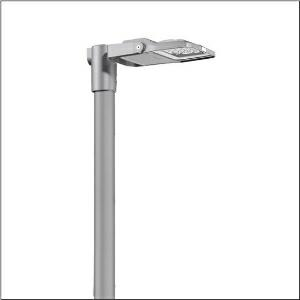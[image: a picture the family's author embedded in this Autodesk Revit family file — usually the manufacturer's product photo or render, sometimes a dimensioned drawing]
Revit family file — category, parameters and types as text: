
# Revit family: floodlight_fl_21_iq_micro___pl61_5xa7762a4c3a_196d
name_source: partatom
category: Lighting Fixtures
units: mm (PartAtom-declared; Revit-internal decimal feet)

## family parameters
Cut with Voids When Loaded = No
Host = Face
Light Source = No
Part Type = Normal
Room Calculation Point = No
Round Connector Dimension = Use Diameter
Shared = No

## types (1)
- --- (1 x LED, 3030 lm, 23.1 W, 4000K)
    Apparent Load = 23 VA
    CIE Flux Codes = 33 65 98 100 100
    Color Rendering = 70
    Color Temperature = 4000K
    Default Elevation = 1800 mm
    Description = Floodlight FL 21 iQ micro, floodlight, primary light control with lens, of PMMA, primary optical cover: protective disc, of toughened safety glass, transparent, light distribution: PL61, light emission: direct distribution, installation type: surface-mounted, lamps: LED, High Power LED, rated values: 3.030lm | 23,1W | 131,2lm/W (begin service life); end service life: 3.030lm | 23,8W; at 50% lumin. flux: 1.515lm | 11W | 137,7lm/W, colour temperature: 4000K, colour rendering: CRI > 70, light colour: 740, light setting 1 begin service life: 100% | 3.030lm | 23,1W | 131,2lm/W | 4.000K, light setting 1 end service life: 23,8W, further light settings possible, control: Auto-Match, Temp-Guard, Night-Set, Smart-Wire, Desk-Remote (wireless, voltage-free reading and setting of iQ features in the workshop via application-optimized NFC function/RFID function), optimised constant luminous flux control (CLO 2.0), Street-Remote, pre-setting: linear dimming characteristic, with terminal, 6-pole, mains connection: 220..240V, AC, 50/60Hz, luminaire housing, of diecast aluminium, powder-coated, SITECO metallic grey (DB 702S), corrosivity category C5 mid according to DIN EN ISO 12944suitable for swimming poolschlorine-resistant, sealing non-destructively replaceable, please order mast flange separately, mast bracket, of steel, galvanised, powder-coated, SITECO metallic grey (DB 702S), protection rating (complete): IP66, insulation class (complete): insulation class II (safety insulation), certification: CE, ENEC, VDE, protection symbol: D, impact resistance: IK07, permissible operating ambient temperature: -40..+40°C, permissible operating ambient temperature for outdoor applications: -40..+50°C, standard: DIN EN 12944, LABS conformity tested according to VDMA 24364:2018-05, packaging unit: 1 piece

Light Distribution: PL61
    Height = 65 mm
    Lamp = 1 x LED
    Lamp Light Flux = 3030 lm
    Lamp Power = 23.1 W
    Lamp count = 1
    Length = 312 mm
    Luminous efficacy = 131 lm/W
    Manufacturer = Siteco
    ModVariant = No
    Model = 5XA7762A4C3A
    Number of Poles = 1
    OnlyDefault = Yes
    Power Factor = 1
    Product Name = Floodlight FL 21 iQ micro | PL61
    Product group = floodlight | pylon annexe
    ProductGroupID = 6201
    Protection Class = Protection class II
    Protection Degree = IP 66
    RLX_Detail_Level = 1
    RLX_Emergency_Light_Flux = 0 lm
    RLX_Emergency_Type = 0
    RLX_Emergency_Type_DB = No
    RlxData = <blob elided: 102197 chars, md5=f2221ea7>
    Socket = socket
    Standby Power = 0 W
    System Light Flux = 3030 lm
    System Power = 23 W
    Type Comments = factory setting: luminous flux: 100 % | dim-lin: 254 | 455 mA
    Type Image = l_1007121.jpg
    URL = http://relux.com
    VarID = @adj_191725
    Voltage = 0 V
    Weight = 0.00 kg
    Width = 230 mm

## geometry (parser evidence)
native form markers: Blend x4, Sweep x10
no freeform markers — native parametric forms only
